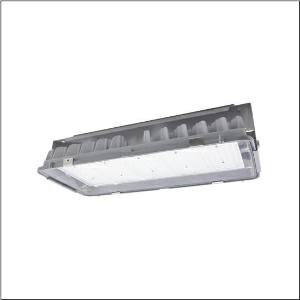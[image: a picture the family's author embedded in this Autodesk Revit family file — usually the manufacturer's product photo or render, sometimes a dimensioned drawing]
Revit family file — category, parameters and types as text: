
# Revit family: highbay_11xtreme_51hf81da4nma
name_source: partatom
category: Lighting Fixtures
units: mm (PartAtom-declared; Revit-internal decimal feet)

## family parameters
Cut with Voids When Loaded = No
Host = Face
Light Source = No
Part Type = Normal
Room Calculation Point = No
Round Connector Dimension = Use Diameter
Shared = No

## types (1)
- --- (1 x LED, 34200 lm, 188.1 W, 4000K)
    Apparent Load = 188 VA
    CIE Flux Codes = 88 96 99 100 100
    Color Rendering = 80
    Color Temperature = 4000K
    Default Elevation = 1800 mm
    Description = Highbay 11Xtreme, LED high bay luminaire, primary light control with lens, of PMMA, primary optical cover: cover, of toughened safety glass, light emission: direct distribution, primary light characteristic: symmetric, installation type: suspended mounting, surface-mounted, 1x LED module,for 1x LED, rated luminous flux: 34.200lm, luminous efficacy: 182lm/W, light colour: 840, colour temperature: 4000K, with cable H07RN-F 5x 1.5mm², mains connection: 220..240V, AC, 50/60Hz, cable length: 1,5m, rated input power: 188W, luminaire housing, of diecast aluminium, partly coated, silver, length: 595mm, width: 280mm, height: 195mm, protection rating (complete): IP66, insulation class (complete): insulation class I (protective earthing), certification: CE, ENEC, UKCA, protection symbol: D, ball protection: ball impact resistant according to DIN VDE 0710 part 13 (with chain suspension), impact resistance: IK08, permissible operating ambient temperature: -25..+45°C, reducing of maximum allowable ambient temperature of 5°C with ceiling mounting, packaging unit: 1 piece
    Height = 157 mm
    Lamp = 1 x LED
    Lamp Light Flux = 34200 lm
    Lamp Power = 188.1 W
    Lamp count = 1
    Length = 593 mm
    Luminous efficacy = 182 lm/W
    Manufacturer = Siteco
    ModVariant = No
    Model = 51HF81DA4NMA
    Mounting Place = Ceiling
    Mounting Type = Pendant
    Number of Poles = 1
    OnlyDefault = Yes
    Power Factor = 1
    Product Name = Highbay 11Xtreme
    Product group = LED high bay luminaire
    ProductGroupID = 903
    Protection Class = Protection class I
    Protection Degree = IP 66
    RLX_Detail_Level = 1
    RLX_Emergency_Light_Flux = 0 lm
    RLX_Emergency_Type = 0
    RLX_Emergency_Type_DB = No
    RlxData = <blob elided: 27833 chars, md5=6f0f6f28>
    Socket = socket
    Standby Power = 0 W
    System Light Flux = 34200 lm
    System Power = 188 W
    Type Comments = factory setting: luminous flux: 100 % | dim-lin: 254 | 1258 mA
    Type Image = l_1258342.jpg
    URL = http://relux.com
    VarID = @adj_053019
    Voltage = 0 V
    Weight = 0.00 kg
    Width = 278 mm

## geometry (parser evidence)
native form markers: Blend x4, Sweep x11
no freeform markers — native parametric forms only
